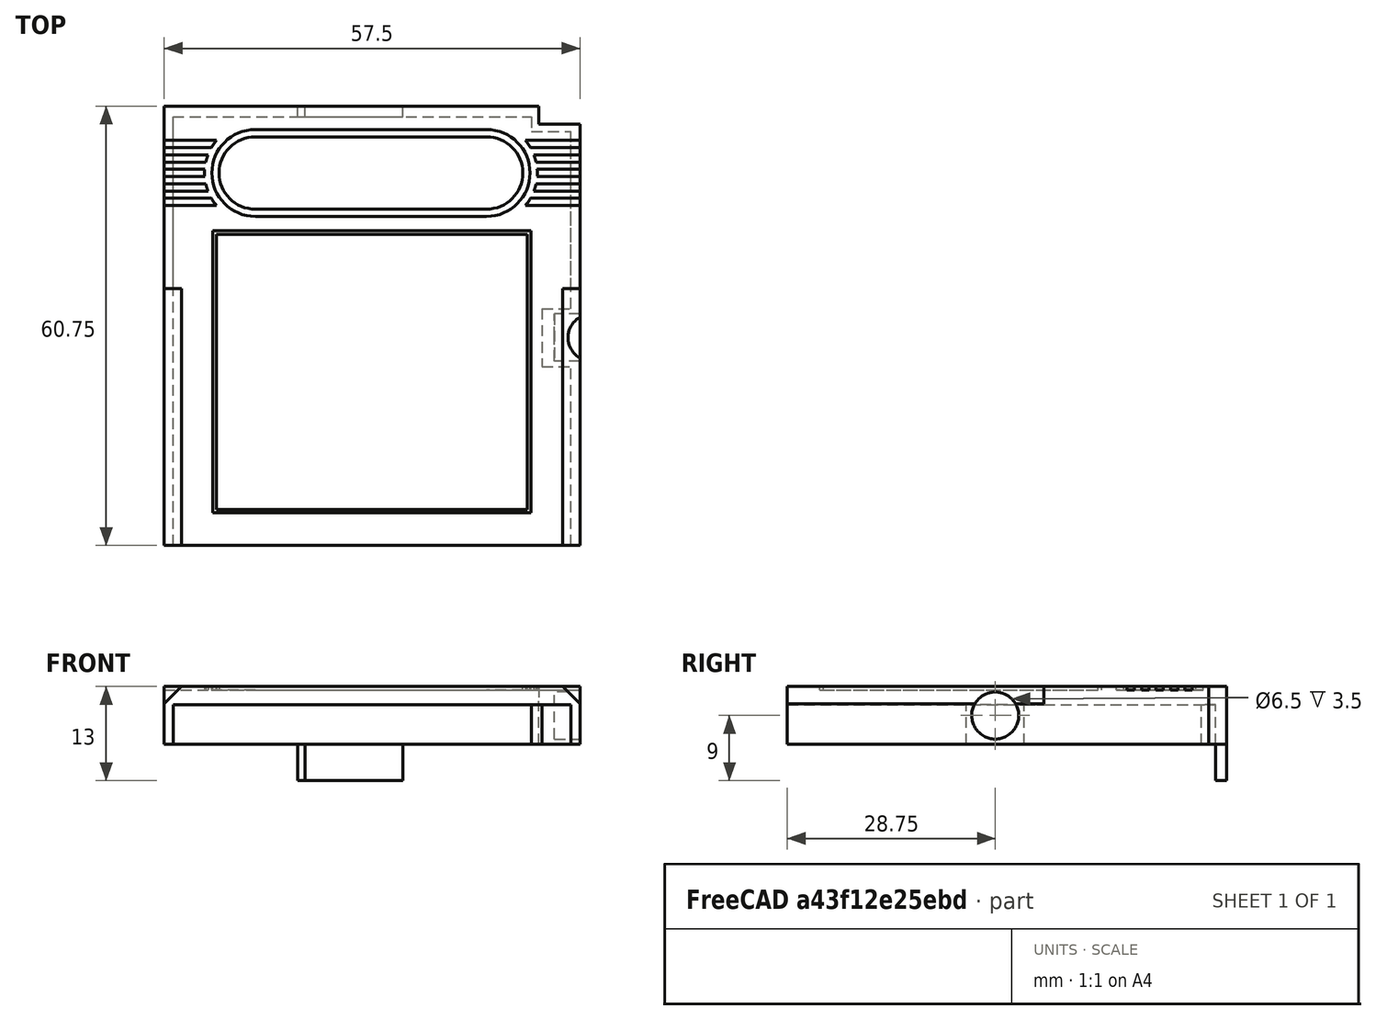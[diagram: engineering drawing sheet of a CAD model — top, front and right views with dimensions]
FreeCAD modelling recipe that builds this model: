
FCSTD DOCUMENT  (FreeCAD 1.0R39109 (Git))
Label: GBC_gameboy_cart_cover
License: All rights reserved
LicenseURL: http://en.wikipedia.org/wiki/All_rights_reserved
objects: Part::Box×24, Part::Cut×12, Part::Cylinder×7, Part::MultiFuse×6, Part::Chamfer×1
note: 50 computed .brp shape members not serialized (recipe doc carries the construction recipe); baked Part::Feature solids carry a one-line shape summary decoded from their .brp

FEATURE [Part::Box] Box  label="Cube(outer_base)"
  AttacherType = Attacher::AttachEngine3D
  Height = 5.5
  Length = 57.5
  Placement = pos=(0,3.5,-0.7) rot=(0,0,1;0rad)
  Width = 60.75
FEATURE [Part::Box] Box001  label="Cube(corner_inner)"
  AttacherType = Attacher::AttachEngine3D
  Height = 6
  Length = 5.7
  Placement = pos=(51.8,61.75,-0.7) rot=(0,0,1;0rad)
  Width = 2.5
FEATURE [Part::Box] Box002  label="Cube(inner_base)"
  AttacherType = Attacher::AttachEngine3D
  Height = 5.5
  Length = 55
  Placement = pos=(1.25,0,-0.7) rot=(0,0,1;0rad)
  Width = 62.75
FEATURE [Part::Box] Box003  label="Cube(corner_outer)"
  AttacherType = Attacher::AttachEngine3D
  Height = 6
  Length = 5.5
  Placement = pos=(50.8,60.75,-0.7) rot=(0,0,1;0rad)
  Width = 3.5
FEATURE [Part::Box] Box017  label="Cube(game_lable_inner)"
  AttacherType = Attacher::AttachEngine3D
  Height = 0.5
  Length = 43
  Placement = pos=(7.25,8.5,6.8) rot=(0,0,1;0rad)
  Width = 38
FEATURE [Part::Cut] Cut
  Base = -> Box
  Tool = -> Box002
FEATURE [Part::MultiFuse] Fusion
  Shapes = -> [Cut,Box003]
FEATURE [Part::Cut] Cut024
  Base = -> Fusion
  Tool = -> Box001
FEATURE [Part::Box] Box056  label="Cube(sd_card_cover)"
  AttacherType = Attacher::AttachEngine3D
  Height = 5
  Length = 13.5
  Placement = pos=(19.5,62.75,-5.7) rot=(0,0,1;0rad)
  Width = 1.5
FEATURE [Part::Box] Box057  label="Cube(magnet_black)"
  AttacherType = Attacher::AttachEngine3D
  Height = 6
  Length = 4
  Placement = pos=(52.25,28.25,-0.7) rot=(0,0,1;0rad)
  Width = 8
FEATURE [Part::Cylinder] Cylinder  label="Cylinder(magnet)"
  Angle = 360
  AttacherType = Attacher::AttachEngine3D
  FirstAngle = 0
  Height = 3.5
  Placement = pos=(54,32.25,3.3) rot=(0,1,0;1.5708rad)
  Radius = 3.25
  SecondAngle = 0
FEATURE [Part::Box] Box041  label="Cube(game_lable_outer)"
  AttacherType = Attacher::AttachEngine3D
  Height = 0.5
  Length = 44
  Placement = pos=(6.75,8,6.8) rot=(0,0,1;0rad)
  Width = 39
FEATURE [Part::Box] Box055  label="Cube(middle_nintendo_inner)"
  AttacherType = Attacher::AttachEngine3D
  Height = 0.5
  Length = 32
  Placement = pos=(12.6,50,6.8) rot=(0,0,1;0rad)
  Width = 10
FEATURE [Part::Cylinder] Cylinder011  label="Cylinder002(right_nintendo_inner)"
  Angle = 360
  AttacherType = Attacher::AttachEngine3D
  FirstAngle = 0
  Height = 0.5
  Placement = pos=(44.6,55,6.8) rot=(0,0,1;0rad)
  Radius = 5
  SecondAngle = 0
FEATURE [Part::Cylinder] Cylinder010  label="Cylinder001(left_nintendo_inner)"
  Angle = 360
  AttacherType = Attacher::AttachEngine3D
  FirstAngle = 0
  Height = 0.5
  Placement = pos=(12.6,55,6.8) rot=(0,0,1;0rad)
  Radius = 5
  SecondAngle = 0
FEATURE [Part::MultiFuse] Fusion033
  Shapes = -> [Cylinder010,Cylinder011,Box055]
FEATURE [Part::Box] Box008  label="Cube001(top_cover_bottom_half)"
  AttacherType = Attacher::AttachEngine3D
  Height = 2.5
  Length = 57.5
  Placement = pos=(0,3.5,4.8) rot=(0,0,1;0rad)
  Width = 35.5
FEATURE [Part::Box] Box044  label="Cube(middle_nintendo_outer)"
  AttacherType = Attacher::AttachEngine3D
  Height = 1
  Length = 32
  Placement = pos=(12.6,49,6.8) rot=(0,0,1;0rad)
  Width = 12
FEATURE [Part::Cylinder] Cylinder007  label="Cylinder002(right_nintendo_outer)"
  Angle = 360
  AttacherType = Attacher::AttachEngine3D
  FirstAngle = 0
  Height = 1
  Placement = pos=(44.6,55,6.8) rot=(0,0,1;0rad)
  Radius = 6
  SecondAngle = 0
FEATURE [Part::Cylinder] Cylinder006  label="Cylinder001(left_nintendo_outer)"
  Angle = 360
  AttacherType = Attacher::AttachEngine3D
  FirstAngle = 0
  Height = 1
  Placement = pos=(12.6,55,6.8) rot=(0,0,1;0rad)
  Radius = 6
  SecondAngle = 0
FEATURE [Part::Cylinder] Cylinder008  label="Cylinder001(left_nintendo_fin_cut)"
  Angle = 360
  AttacherType = Attacher::AttachEngine3D
  FirstAngle = 0
  Height = 1
  Placement = pos=(12.6,55,6.8) rot=(0,0,1;0rad)
  Radius = 7
  SecondAngle = 0
FEATURE [Part::Box] Box046  label="Cube001(left_fin_5)"
  AttacherType = Attacher::AttachEngine3D
  Height = 1
  Length = 10
  Placement = pos=(0,52.5,6.8) rot=(0,0,1;0rad)
  Width = 1
FEATURE [Part::Box] Box048  label="Cube003(left_fin_4)"
  AttacherType = Attacher::AttachEngine3D
  Height = 1
  Length = 10
  Placement = pos=(0,56.5,6.8) rot=(0,0,1;0rad)
  Width = 1
FEATURE [Part::Box] Box049  label="Cube004(left_fin_3)"
  AttacherType = Attacher::AttachEngine3D
  Height = 1
  Length = 10
  Placement = pos=(0,58.5,6.8) rot=(0,0,1;0rad)
  Width = 1
FEATURE [Part::Box] Box047  label="Cube002(left_fin_2)"
  AttacherType = Attacher::AttachEngine3D
  Height = 1
  Length = 10
  Placement = pos=(0,54.5,6.8) rot=(0,0,1;0rad)
  Width = 1
FEATURE [Part::Box] Box045  label="Cube(left_fin_1)"
  AttacherType = Attacher::AttachEngine3D
  Height = 1
  Length = 10
  Placement = pos=(0,50.5,6.8) rot=(0,0,1;0rad)
  Width = 1
FEATURE [Part::MultiFuse] Fusion004
  Shapes = -> [Box045,Box047,Box049,Box048,Box046]
FEATURE [Part::Cut] Cut009
  Base = -> Fusion004
  Tool = -> Cylinder008
FEATURE [Part::Cylinder] Cylinder009  label="Cylinder002(right_nintendo_fin_cut)"
  Angle = 360
  AttacherType = Attacher::AttachEngine3D
  FirstAngle = 0
  Height = 1
  Placement = pos=(44.6,55,6.8) rot=(0,0,1;0rad)
  Radius = 7
  SecondAngle = 0
FEATURE [Part::Box] Box052  label="Cube004(right_fin_3)"
  AttacherType = Attacher::AttachEngine3D
  Height = 1
  Length = 10
  Placement = pos=(47.5,58.5,6.8) rot=(0,0,1;0rad)
  Width = 1
FEATURE [Part::Box] Box053  label="Cube003(right_fin_4)"
  AttacherType = Attacher::AttachEngine3D
  Height = 1
  Length = 10
  Placement = pos=(47.5,56.5,6.8) rot=(0,0,1;0rad)
  Width = 1
FEATURE [Part::Box] Box054  label="Cube001(right_fin_5)"
  AttacherType = Attacher::AttachEngine3D
  Height = 1
  Length = 10
  Placement = pos=(47.5,52.5,6.8) rot=(0,0,1;0rad)
  Width = 1
FEATURE [Part::Box] Box051  label="Cube002(right_fin_2)"
  AttacherType = Attacher::AttachEngine3D
  Height = 1
  Length = 10
  Placement = pos=(47.5,54.5,6.8) rot=(0,0,1;0rad)
  Width = 1
FEATURE [Part::Box] Box050  label="Cube(right_fin_1)"
  AttacherType = Attacher::AttachEngine3D
  Height = 1
  Length = 10
  Placement = pos=(47.5,50.5,6.8) rot=(0,0,1;0rad)
  Width = 1
FEATURE [Part::MultiFuse] Fusion003
  Shapes = -> [Box050,Box051,Box054,Box053,Box052]
FEATURE [Part::Cut] Cut008
  Base = -> Fusion003
  Tool = -> Cylinder009
FEATURE [Part::Box] Box010  label="Cube(top_corner_cut)"
  AttacherType = Attacher::AttachEngine3D
  Height = 10
  Length = 10
  Placement = pos=(51.8,61.75,0) rot=(0,0,1;0rad)
  Width = 10
FEATURE [Part::Box] Box007  label="Cube(top_cover_top_half)"
  AttacherType = Attacher::AttachEngine3D
  Height = 2.5
  Length = 57.5
  Placement = pos=(0,39,4.8) rot=(0,0,1;0rad)
  Width = 25.25
FEATURE [Part::Cut] Cut006
  Base = -> Box007
  Tool = -> Box010
FEATURE [Part::Cut] Cut010
  Base = -> Cut006
  Tool = -> Cut008
FEATURE [Part::Cut] Cut011
  Base = -> Cut010
  Tool = -> Cut009
FEATURE [Part::Cut] Cut012
  Base = -> Cut011
  Tool = -> Cylinder006
FEATURE [Part::Cut] Cut013
  Base = -> Cut012
  Tool = -> Cylinder007
FEATURE [Part::Cut] Cut014
  Base = -> Cut013
  Tool = -> Box044
FEATURE [Part::Chamfer] Chamfer
  Base = -> Box008
  EdgeLinks = -> Box008 [Edge2,Edge6]
  Edges = 2 edges r=2.4: [Edge2,Edge6]
FEATURE [Part::MultiFuse] Fusion034
  Shapes = -> [Box057,Chamfer,Cut024,Fusion033,Cut014]
FEATURE [Part::Cut] Cut025
  Base = -> Fusion034
  Tool = -> Cylinder
FEATURE [Part::Cut] Cut026
  Base = -> Cut025
  Tool = -> Box041
FEATURE [Part::MultiFuse] Fusion035
  Shapes = -> [Cut026,Box017]
FEATURE [Part::Box] Box058  label="Cube(sd_card_cover)001"
  AttacherType = Attacher::AttachEngine3D
  Height = 5
  Length = 14.5
  Placement = pos=(18.5,62.75,-5.7) rot=(0,0,1;0rad)
  Width = 1.5
